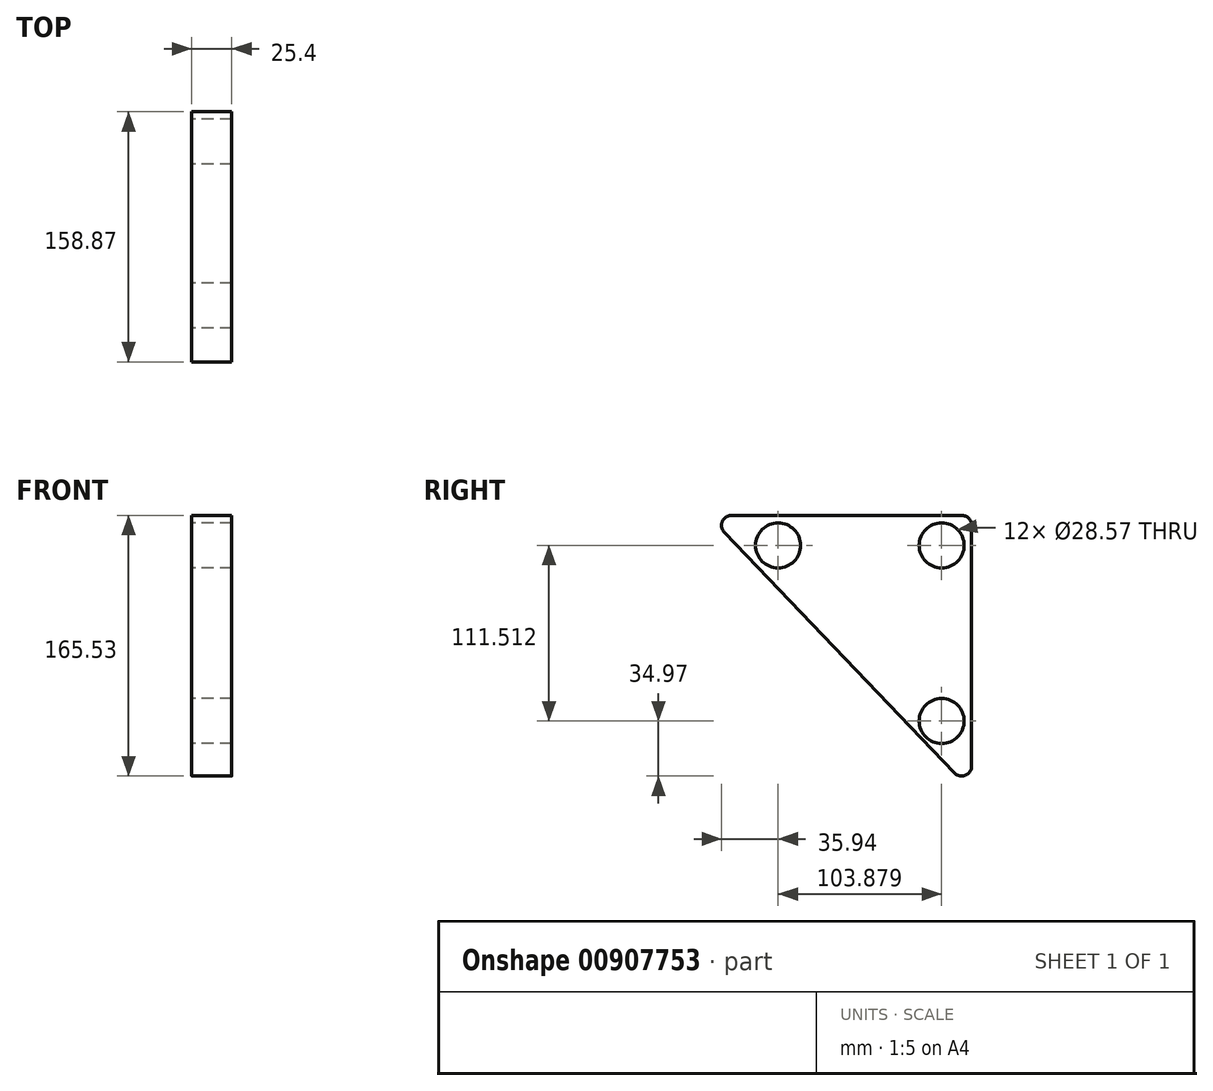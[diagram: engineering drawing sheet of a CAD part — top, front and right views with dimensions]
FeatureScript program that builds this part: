
annotation { "Feature Type Name" : "Feature", "Feature Type Description" : "" }
export const myFeature = defineFeature(function(context is Context, id is Id, definition is map)
    precondition{}
    {
        {
            var Q0;
            Q0=qCreatedBy(makeId("Right.planeOp"),FACE);
            var sketch = newSketch(context, id + "F0", { "sketchPlane" : qUnion([Q0])});
            skLineSegment(sketch, "E0.top", {"start": v(14.86, 175.01) * mm, "end": v(161.03, 175.01) * mm});
            skLineSegment(sketch, "E0.right", {"start": v(167.38, 15.83) * mm, "end": v(167.38, 168.66) * mm});
            skCircle(sketch, "E1", {"center": v(44.45, 155.96) * mm, "radius": 14.29 * mm});
            skCircle(sketch, "E2", {"center": v(148.33, 44.45) * mm, "radius": 14.29 * mm});
            skLineSegment(sketch, "E3", {"start": v(44.45, 155.96) * mm, "end": v(269.6, 155.96) * mm, "construction": true});
            skLineSegment(sketch, "E4", {"start": v(148.33, 44.45) * mm, "end": v(148.33, 224.45) * mm, "construction": true});
            skCircle(sketch, "E5", {"center": v(148.33, 155.96) * mm, "radius": 14.29 * mm});
            skLineSegment(sketch, "E6", {"start": v(10.27, 164.27) * mm, "end": v(156.44, 11.44) * mm});
            skPoint(sketch, "E7.visualSharp", {"position": v(0, 175.01) * mm});
            skArc(sketch, "E7.filletArc", {"start": v(14.86, 175.01) * mm, "mid": v(9.02, 171.16) * mm, "end": v(10.27, 164.27) * mm});
            skPoint(sketch, "E8.visualSharp", {"position": v(167.38, 175.01) * mm});
            skArc(sketch, "E8.filletArc", {"start": v(167.38, 168.66) * mm, "mid": v(165.52, 173.15) * mm, "end": v(161.03, 175.01) * mm});
            skPoint(sketch, "E9.visualSharp", {"position": v(167.38, 0) * mm});
            skArc(sketch, "E9.filletArc", {"start": v(156.44, 11.44) * mm, "mid": v(163.4, 9.93) * mm, "end": v(167.38, 15.83) * mm});
            skSolve(sketch);
        }
        {
            var Q0;
            Q0 = qSketchRegion(id + "F0", true);
            extrude(context, id + "F1", {"entities" : qUnion([Q0]), "depth" : 25.4 * mm, "offsetDistance" : 25.4 * mm});
        }
    });
